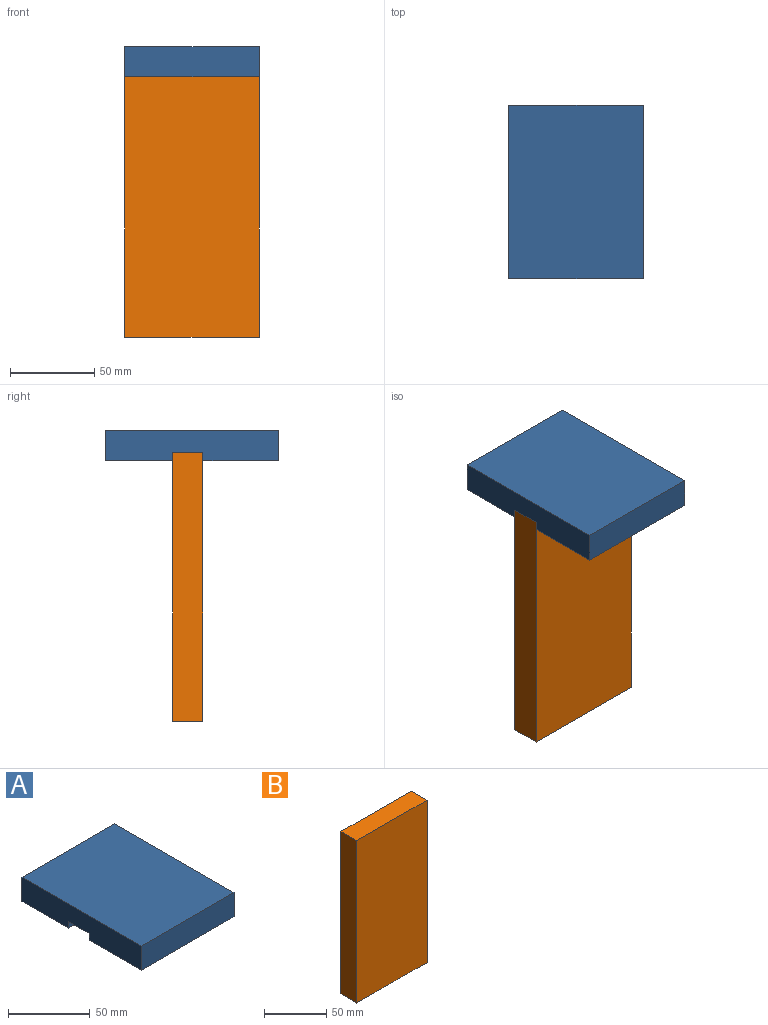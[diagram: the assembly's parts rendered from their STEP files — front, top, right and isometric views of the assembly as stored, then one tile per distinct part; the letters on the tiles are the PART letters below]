
ASSEMBLY  parts=2 mates=1
PART A: 10 faces, bbox 80x103x18 mm
  f0: plane 80x45mm, normal (0,0,-1), area 3600mm2, adj f1,f2,f3,f7
  f1: plane 103x18mm, normal (1,0,0), area 1764mm2, adj f0,f3,f4,f5,f6,f7,f8,f9
  f2: plane 103x18mm, normal (-1,0,0), area 1764mm2, adj f0,f3,f4,f5,f6,f7,f8,f9
  f3: plane 80x18mm, normal (0,-1,0), area 1440mm2, adj f0,f1,f2,f5
  f4: plane 80x18mm, normal (0,1,0), area 1440mm2, adj f1,f2,f5,f6
  f5: plane 103x80mm, normal (0,0,1), area 8240mm2, adj f1,f2,f3,f4
  f6: plane 80x40mm, normal (0,0,-1), area 3200mm2, adj f1,f2,f4,f8
  f7: plane 80x5mm, normal (0,1,0), area 400mm2, adj f0,f1,f2,f9
  f8: plane 80x5mm, normal (0,-1,0), area 400mm2, adj f1,f2,f6,f9
  f9: plane 80x18mm, normal (0,0,-1), area 1440mm2, adj f1,f2,f7,f8
PART B: 6 faces, bbox 80x18x160 mm
  f0: plane 80x18mm, normal (0,0,1), area 1440mm2, adj f1,f3,f4,f5
  f1: plane 160x18mm, normal (-1,0,0), area 2880mm2, adj f0,f2,f4,f5
  f2: plane 80x18mm, normal (0,0,-1), area 1440mm2, adj f1,f3,f4,f5
  f3: plane 160x18mm, normal (1,0,0), area 2880mm2, adj f0,f2,f4,f5
  f4: plane 160x80mm, normal (0,-1,0), area 12800mm2, adj f0,f1,f2,f3
  f5: plane 160x80mm, normal (0,1,0), area 12800mm2, adj f0,f1,f2,f3
PLACE A t=(0,-11.5,75)mm
PLACE B at identity
MATE fastened A.f9 <-> B.f0  axis (0,0,1) through (40,0,80)mm
